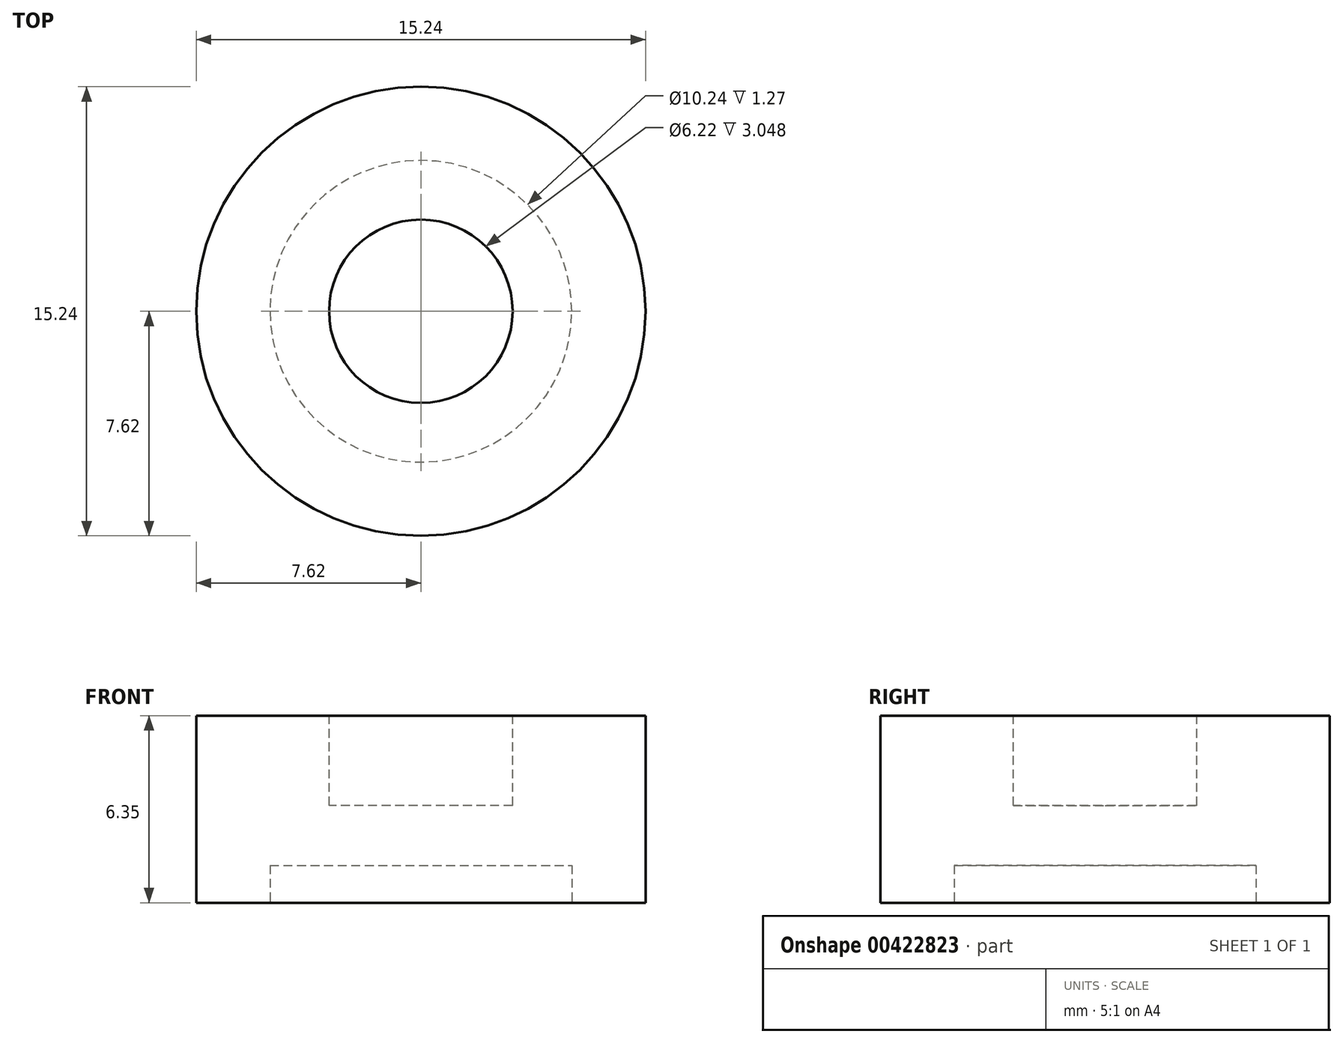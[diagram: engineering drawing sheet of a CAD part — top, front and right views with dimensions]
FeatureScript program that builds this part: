
annotation { "Feature Type Name" : "Feature", "Feature Type Description" : "" }
export const myFeature = defineFeature(function(context is Context, id is Id, definition is map)
    precondition{}
    {
        {
            var Q0;
            Q0=qCreatedBy(makeId("Top.planeOp"),FACE);
            var sketch = newSketch(context, id + "F0", { "sketchPlane" : qUnion([Q0])});
            skCircle(sketch, "E0", {"center": v(0, 0) * mm, "radius": 7.62 * mm});
            skSolve(sketch);
        }
        {
            var Q0;
            Q0 = qSketchRegion(id + "F0", true);
            extrude(context, id + "F1", {"entities" : qUnion([Q0]), "depth" : 6.35 * mm});
        }
        {
            var Q0;
            Q0=makeQuery(id+"F1.opExtrude","CAP_FACE",FACE,{"disambiguationData":[OSD([sQuery(id+"F0.wireOp",EDGE,"E0")])],"isStart":true});
            var sketch = newSketch(context, id + "F2", { "sketchPlane" : qUnion([Q0])});
            skCircle(sketch, "E1", {"center": v(0, 0) * mm, "radius": 5.12 * mm});
            skSolve(sketch);
        }
        {
            var Q0;
            Q0 = qSketchRegion(id + "F2", true);
            extrude(context, id + "F3", {"entities" : qUnion([Q0]), "operationType" : NewBodyOperationType.REMOVE, "oppositeDirection" : true, "depth" : 1.27 * mm});
        }
        {
            var Q0;
            Q0=makeQuery(id+"F1.opExtrude","CAP_FACE",FACE,{"disambiguationData":[OSD([sQuery(id+"F0.wireOp",EDGE,"E0")])],"isStart":false});
            var sketch = newSketch(context, id + "F4", { "sketchPlane" : qUnion([Q0])});
            skCircle(sketch, "E2", {"center": v(0, 0) * mm, "radius": 3.11 * mm});
            skSolve(sketch);
        }
        {
            var Q0;
            Q0 = qSketchRegion(id + "F4", true);
            extrude(context, id + "F5", {"entities" : qUnion([Q0]), "operationType" : NewBodyOperationType.REMOVE, "oppositeDirection" : true, "depth" : 3.05 * mm});
        }
    });
